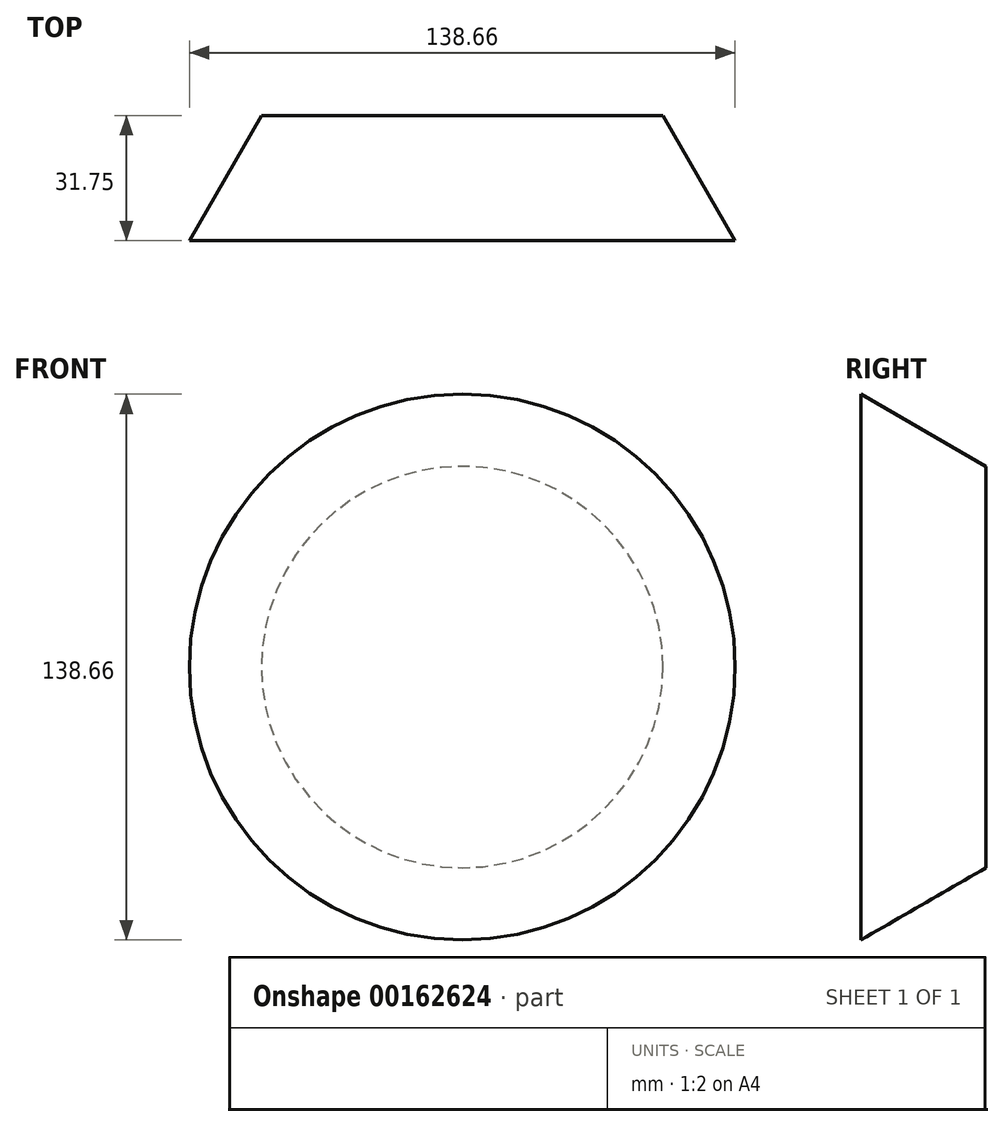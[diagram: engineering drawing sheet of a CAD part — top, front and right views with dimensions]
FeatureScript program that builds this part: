
annotation { "Feature Type Name" : "Feature", "Feature Type Description" : "" }
export const myFeature = defineFeature(function(context is Context, id is Id, definition is map)
    precondition{}
    {
        {
            var Q0;
            Q0=qCreatedBy(makeId("Front.planeOp"),FACE);
            var sketch = newSketch(context, id + "F0", { "sketchPlane" : qUnion([Q0])});
            skCircle(sketch, "E0", {"center": v(0, 0) * mm, "radius": 51 * mm});
            skSolve(sketch);
        }
        {
            var Q0;
            Q0=makeQuery(id+"F0.imprint","IMPRINT",FACE,{"disambiguationData":[TD([[makeQuery(id+"F0.imprint","IMPRINT",EDGE,{"derivedFrom":sQuery(id+"F0.wireOp",EDGE,"E0")}),1.0]])]});
            extrude(context, id + "F1", {"entities" : qUnion([Q0]), "depth" : 31.75 * mm, "hasDraft" : true, "draftAngle" : 30 * degree});
        }
    });
